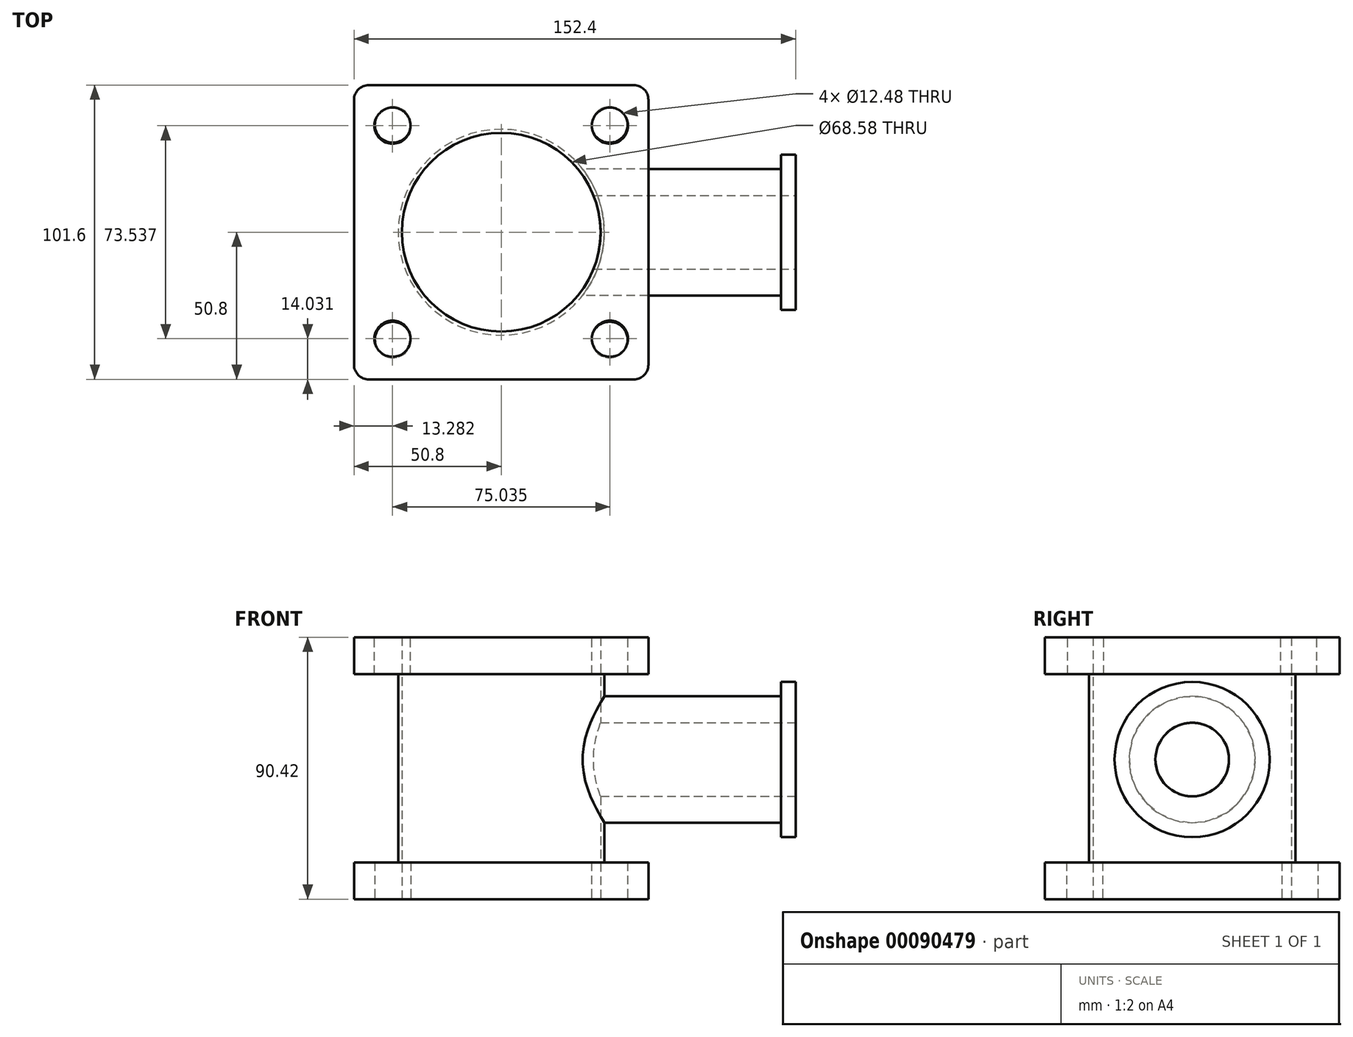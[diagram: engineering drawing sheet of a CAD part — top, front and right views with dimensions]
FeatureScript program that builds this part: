
annotation { "Feature Type Name" : "Feature", "Feature Type Description" : "" }
export const myFeature = defineFeature(function(context is Context, id is Id, definition is map)
    precondition{}
    {
        {
            var Q0;
            Q0=qCreatedBy(makeId("Top.planeOp"),FACE);
            var sketch = newSketch(context, id + "F0", { "sketchPlane" : qUnion([Q0])});
            skLineSegment(sketch, "E0.bottom", {"start": v(50.8, -50.8) * mm, "end": v(-50.8, -50.8) * mm});
            skLineSegment(sketch, "E0.top", {"start": v(50.8, 50.8) * mm, "end": v(-50.8, 50.8) * mm});
            skLineSegment(sketch, "E0.left", {"start": v(50.8, -50.8) * mm, "end": v(50.8, 50.8) * mm});
            skLineSegment(sketch, "E0.right", {"start": v(-50.8, -50.8) * mm, "end": v(-50.8, 50.8) * mm});
            skPoint(sketch, "E0.middle", {"position": v(0, 0) * mm});
            skSolve(sketch);
        }
        {
            var Q0;
            Q0 = qSketchRegion(id + "F0", true);
            extrude(context, id + "F1", {"entities" : qUnion([Q0]), "depth" : 12.7 * mm});
        }
        {
            var Q0;
            Q0=makeQuery(id+"F1.opExtrude","CAP_FACE",FACE,{"disambiguationData":[OSD([sQuery(id+"F0.wireOp",EDGE,"E0.bottom"),sQuery(id+"F0.wireOp",EDGE,"E0.top"),sQuery(id+"F0.wireOp",EDGE,"E0.left"),sQuery(id+"F0.wireOp",EDGE,"E0.right")])],"isStart":true});
            var sketch = newSketch(context, id + "F2", { "sketchPlane" : qUnion([Q0])});
            skCircle(sketch, "E1", {"center": v(0, 0) * mm, "radius": 35.56 * mm});
            skSolve(sketch);
        }
        {
            var Q0;
            Q0 = qSketchRegion(id + "F2", true);
            extrude(context, id + "F3", {"entities" : qUnion([Q0]), "operationType" : NewBodyOperationType.ADD, "depth" : 65.02 * mm});
        }
        {
            var Q0;
            Q0=makeQuery(id+"F3.opExtrude","CAP_FACE",FACE,{"disambiguationData":[OSD([sQuery(id+"F2.wireOp",EDGE,"E1")])],"isStart":false});
            var sketch = newSketch(context, id + "F4", { "sketchPlane" : qUnion([Q0])});
            skLineSegment(sketch, "E2.bottom", {"start": v(50.8, 50.8) * mm, "end": v(-50.8, 50.8) * mm});
            skLineSegment(sketch, "E2.top", {"start": v(50.8, -50.8) * mm, "end": v(-50.8, -50.8) * mm});
            skLineSegment(sketch, "E2.left", {"start": v(50.8, 50.8) * mm, "end": v(50.8, -50.8) * mm});
            skLineSegment(sketch, "E2.right", {"start": v(-50.8, 50.8) * mm, "end": v(-50.8, -50.8) * mm});
            skPoint(sketch, "E2.middle", {"position": v(0, 0) * mm});
            skSolve(sketch);
        }
        {
            var Q0;
            Q0=makeQuery(id+"F4.imprint","IMPRINT",FACE,{"disambiguationData":[TD([[makeQuery(id+"F4.imprint","IMPRINT",EDGE,{"derivedFrom":makeQuery(id+"F3.opExtrude","CAP_EDGE",EDGE,{"disambiguationData":[OSD([sQuery(id+"F2.wireOp",EDGE,"E1")])],"isStart":false})}),1.0]])]});
            var Q1;
            Q1=makeQuery(id+"F4.imprint","IMPRINT",FACE,{"disambiguationData":[TD([[makeQuery(id+"F4.imprint","IMPRINT",EDGE,{"derivedFrom":sQuery(id+"F4.wireOp",EDGE,"E2.bottom")}),1.0]])]});
            extrude(context, id + "F5", {"entities" : qUnion([Q0, Q1]), "operationType" : NewBodyOperationType.ADD, "depth" : 12.7 * mm});
        }
        {
            var Q0;
            Q0=makeQuery(id+"F1.opExtrude","SWEPT_EDGE",EDGE,{"disambiguationData":[OSD([sQuery(id+"F0.wireOp",EDGE,"E0.bottom"),sQuery(id+"F0.wireOp",EDGE,"E0.left")])]});
            var Q1;
            Q1=makeQuery(id+"F1.opExtrude","SWEPT_EDGE",EDGE,{"disambiguationData":[OSD([sQuery(id+"F0.wireOp",EDGE,"E0.bottom"),sQuery(id+"F0.wireOp",EDGE,"E0.right")])]});
            var Q2;
            Q2=makeQuery(id+"F1.opExtrude","SWEPT_EDGE",EDGE,{"disambiguationData":[OSD([sQuery(id+"F0.wireOp",EDGE,"E0.top"),sQuery(id+"F0.wireOp",EDGE,"E0.left")])]});
            var Q3;
            Q3=makeQuery(id+"F1.opExtrude","SWEPT_EDGE",EDGE,{"disambiguationData":[OSD([sQuery(id+"F0.wireOp",EDGE,"E0.top"),sQuery(id+"F0.wireOp",EDGE,"E0.right")])]});
            var Q4;
            Q4=makeQuery(id+"F5.opExtrude","SWEPT_EDGE",EDGE,{"disambiguationData":[OSD([sQuery(id+"F4.wireOp",EDGE,"E2.top"),sQuery(id+"F4.wireOp",EDGE,"E2.right")])]});
            var Q5;
            Q5=makeQuery(id+"F5.opExtrude","SWEPT_EDGE",EDGE,{"disambiguationData":[OSD([sQuery(id+"F4.wireOp",EDGE,"E2.top"),sQuery(id+"F4.wireOp",EDGE,"E2.left")])]});
            var Q6;
            Q6=makeQuery(id+"F5.opExtrude","SWEPT_EDGE",EDGE,{"disambiguationData":[OSD([sQuery(id+"F4.wireOp",EDGE,"E2.bottom"),sQuery(id+"F4.wireOp",EDGE,"E2.left")])]});
            var Q7;
            Q7=makeQuery(id+"F5.opExtrude","SWEPT_EDGE",EDGE,{"disambiguationData":[OSD([sQuery(id+"F4.wireOp",EDGE,"E2.bottom"),sQuery(id+"F4.wireOp",EDGE,"E2.right")])]});
            fillet(context, id + "F6", {"entities" : qUnion([Q0, Q1, Q2, Q3, Q4, Q5, Q6, Q7]), "radius" : 5.08 * mm, "tangentPropagation" : true, "allowEdgeOverflow" : false});
        }
        {
            var Q0;
            Q0=qCreatedBy(makeId("Right.planeOp"),FACE);
            var sketch = newSketch(context, id + "F7", { "sketchPlane" : qUnion([Q0])});
            skCircle(sketch, "E3", {"center": v(0, -29.54) * mm, "radius": 21.81 * mm});
            skSolve(sketch);
        }
        {
            var Q0;
            Q0 = qSketchRegion(id + "F7", true);
            extrude(context, id + "F8", {"entities" : qUnion([Q0]), "operationType" : NewBodyOperationType.ADD, "depth" : 101.6 * mm});
        }
        {
            var Q0;
            Q0=makeQuery(id+"F8.opExtrude","CAP_FACE",FACE,{"disambiguationData":[OSD([sQuery(id+"F7.wireOp",EDGE,"E3")])],"isStart":false});
            var sketch = newSketch(context, id + "F9", { "sketchPlane" : qUnion([Q0])});
            skCircle(sketch, "E4", {"center": v(0, -29.54) * mm, "radius": 26.8 * mm});
            skSolve(sketch);
        }
        {
            var Q0;
            Q0 = qSketchRegion(id + "F9", true);
            extrude(context, id + "F10", {"entities" : qUnion([Q0]), "operationType" : NewBodyOperationType.ADD, "oppositeDirection" : true, "depth" : 5.08 * mm});
        }
        {
            var Q0;
            Q0=sQuery(id+"F9.wireOp",VERTEX,"E4.center");
            var Q1;
            Q1=makeQuery(id+"F1.opExtrude","SWEPT_BODY",BODY,{"disambiguationData":[OSD([sQuery(id+"F0.wireOp",EDGE,"E0.bottom"),sQuery(id+"F0.wireOp",EDGE,"E0.top"),sQuery(id+"F0.wireOp",EDGE,"E0.left"),sQuery(id+"F0.wireOp",EDGE,"E0.right")])]});
            hole(context, id + "F11", {"style" : HoleStyle.SIMPLE, "endStyle" : HoleEndStyle.BLIND, "holeDiameter" : 25.4 * mm, "holeDepth" : 127 * mm, "locations" : qUnion([Q0]), "scope" : qUnion([Q1])});
        }
        {
            var Q0;
            Q0=makeQuery(id+"F5.opExtrude","CAP_FACE",FACE,{"disambiguationData":[OSD([sQuery(id+"F4.wireOp",EDGE,"E2.bottom"),sQuery(id+"F4.wireOp",EDGE,"E2.top"),sQuery(id+"F4.wireOp",EDGE,"E2.left"),sQuery(id+"F4.wireOp",EDGE,"E2.right")])],"isStart":false});
            var sketch = newSketch(context, id + "F12", { "sketchPlane" : qUnion([Q0])});
            skCircle(sketch, "E5", {"center": v(0, 0) * mm, "radius": 34.3 * mm});
            skSolve(sketch);
        }
        {
            var Q0;
            Q0 = qSketchRegion(id + "F12", true);
            extrude(context, id + "F13", {"entities" : qUnion([Q0]), "operationType" : NewBodyOperationType.REMOVE, "oppositeDirection" : true, "depth" : 91.44 * mm});
        }
        {
            var Q0;
            Q0=makeQuery(id+"F1.opExtrude","CAP_FACE",FACE,{"disambiguationData":[OSD([sQuery(id+"F0.wireOp",EDGE,"E0.bottom"),sQuery(id+"F0.wireOp",EDGE,"E0.top"),sQuery(id+"F0.wireOp",EDGE,"E0.left"),sQuery(id+"F0.wireOp",EDGE,"E0.right")])],"isStart":false});
            var sketch = newSketch(context, id + "F14", { "sketchPlane" : qUnion([Q0])});
            skCircle(sketch, "E6", {"center": v(-37.52, 36.77) * mm, "radius": 6.24 * mm});
            skCircle(sketch, "E7.MirrorC", {"center": v(-37.52, -36.77) * mm, "radius": 6.24 * mm});
            skCircle(sketch, "E8.MirrorC", {"center": v(37.52, 36.77) * mm, "radius": 6.24 * mm});
            skCircle(sketch, "E9.MirrorC", {"center": v(37.52, -36.77) * mm, "radius": 6.24 * mm});
            skSolve(sketch);
        }
        {
            var Q0;
            Q0 = qSketchRegion(id + "F14", true);
            extrude(context, id + "F15", {"entities" : qUnion([Q0]), "operationType" : NewBodyOperationType.REMOVE, "oppositeDirection" : true, "depth" : 12.7 * mm});
        }
        {
            var Q0;
            Q0=makeQuery(id+"F5.opExtrude","CAP_FACE",FACE,{"disambiguationData":[OSD([sQuery(id+"F4.wireOp",EDGE,"E2.bottom"),sQuery(id+"F4.wireOp",EDGE,"E2.top"),sQuery(id+"F4.wireOp",EDGE,"E2.left"),sQuery(id+"F4.wireOp",EDGE,"E2.right")])],"isStart":false});
            var sketch = newSketch(context, id + "F16", { "sketchPlane" : qUnion([Q0])});
            skCircle(sketch, "E10", {"center": v(-37.4, 37.12) * mm, "radius": 6.2 * mm});
            skCircle(sketch, "E11.MirrorC", {"center": v(37.4, 37.12) * mm, "radius": 6.2 * mm});
            skCircle(sketch, "E12.MirrorC", {"center": v(-37.4, -37.12) * mm, "radius": 6.2 * mm});
            skCircle(sketch, "E13.MirrorC", {"center": v(37.4, -37.12) * mm, "radius": 6.2 * mm});
            skSolve(sketch);
        }
        {
            var Q0;
            Q0 = qSketchRegion(id + "F16", true);
            extrude(context, id + "F17", {"entities" : qUnion([Q0]), "operationType" : NewBodyOperationType.REMOVE, "oppositeDirection" : true, "depth" : 12.7 * mm});
        }
    });
